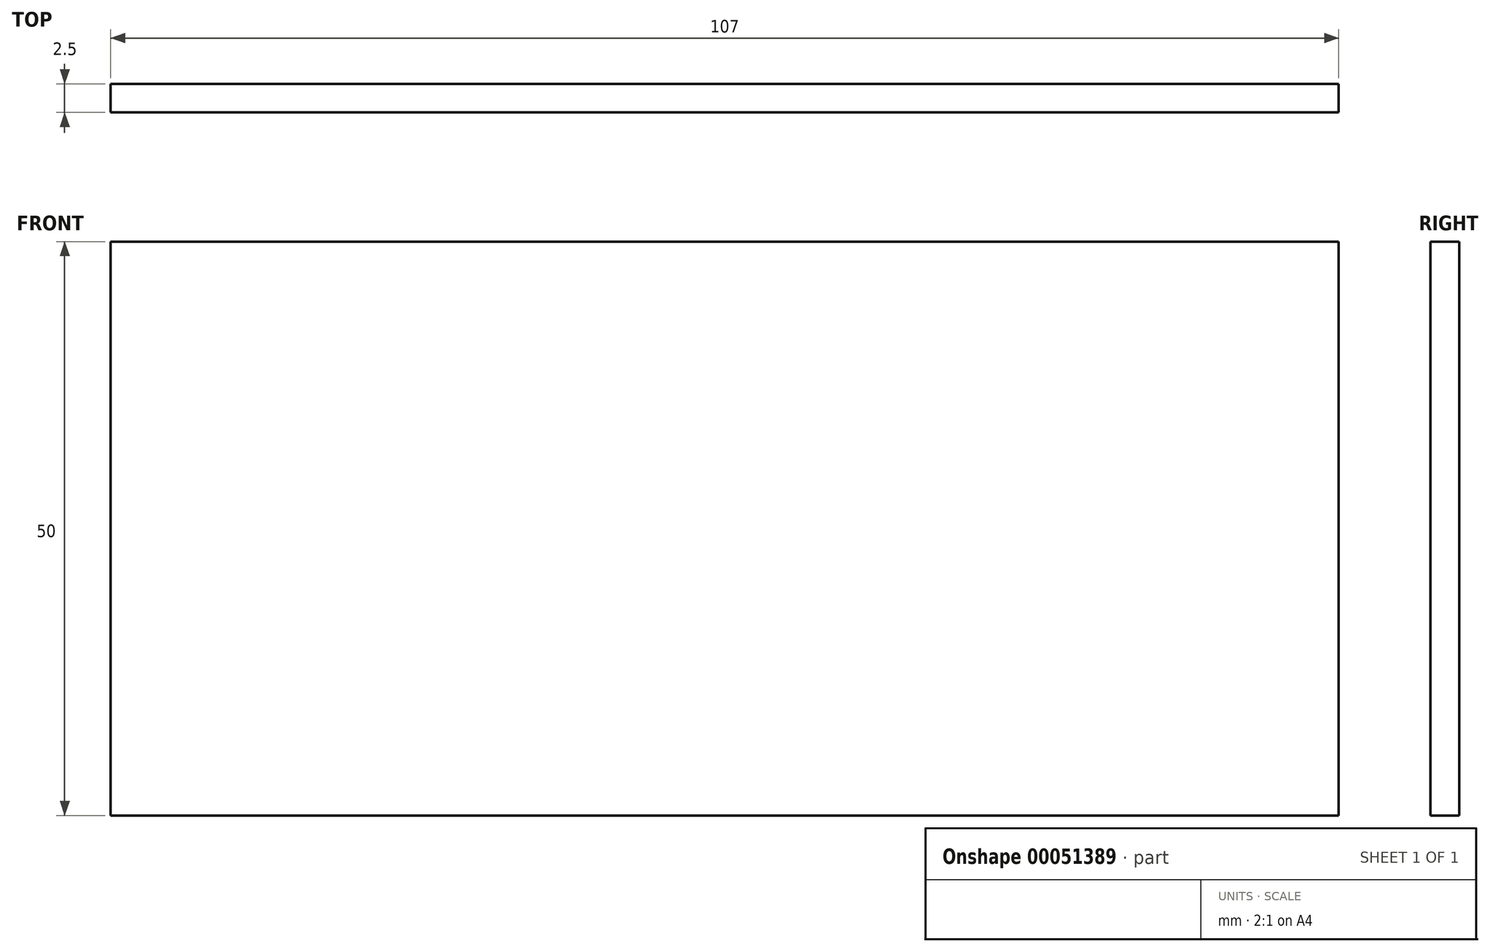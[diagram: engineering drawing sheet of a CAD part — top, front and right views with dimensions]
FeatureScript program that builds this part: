
annotation { "Feature Type Name" : "Feature", "Feature Type Description" : "" }
export const myFeature = defineFeature(function(context is Context, id is Id, definition is map)
    precondition{}
    {
        {
            var Q0;
            Q0=qCreatedBy(makeId("Front.planeOp"),FACE);
            var sketch = newSketch(context, id + "F0", { "sketchPlane" : qUnion([Q0])});
            skLineSegment(sketch, "E0.rect.bottom", {"start": v(53.5, 25) * mm, "end": v(-53.5, 25) * mm});
            skLineSegment(sketch, "E0.rect.top", {"start": v(53.5, -25) * mm, "end": v(-53.5, -25) * mm});
            skLineSegment(sketch, "E0.rect.left", {"start": v(53.5, 25) * mm, "end": v(53.5, -25) * mm});
            skLineSegment(sketch, "E0.rect.right", {"start": v(-53.5, 25) * mm, "end": v(-53.5, -25) * mm});
            skPoint(sketch, "E0.rect.middle", {"position": v(0, 0) * mm});
            skSolve(sketch);
        }
        {
            var Q0;
            Q0=makeQuery(id+"F0.imprint","IMPRINT",FACE,{"disambiguationData":[TD([[makeQuery(id+"F0.imprint","IMPRINT",EDGE,{"derivedFrom":sQuery(id+"F0.wireOp",EDGE,"E0.rect.bottom")}),1.0]])]});
            extrude(context, id + "F1", {"entities" : qUnion([Q0]), "oppositeDirection" : true, "depth" : 2.5 * mm});
        }
    });
